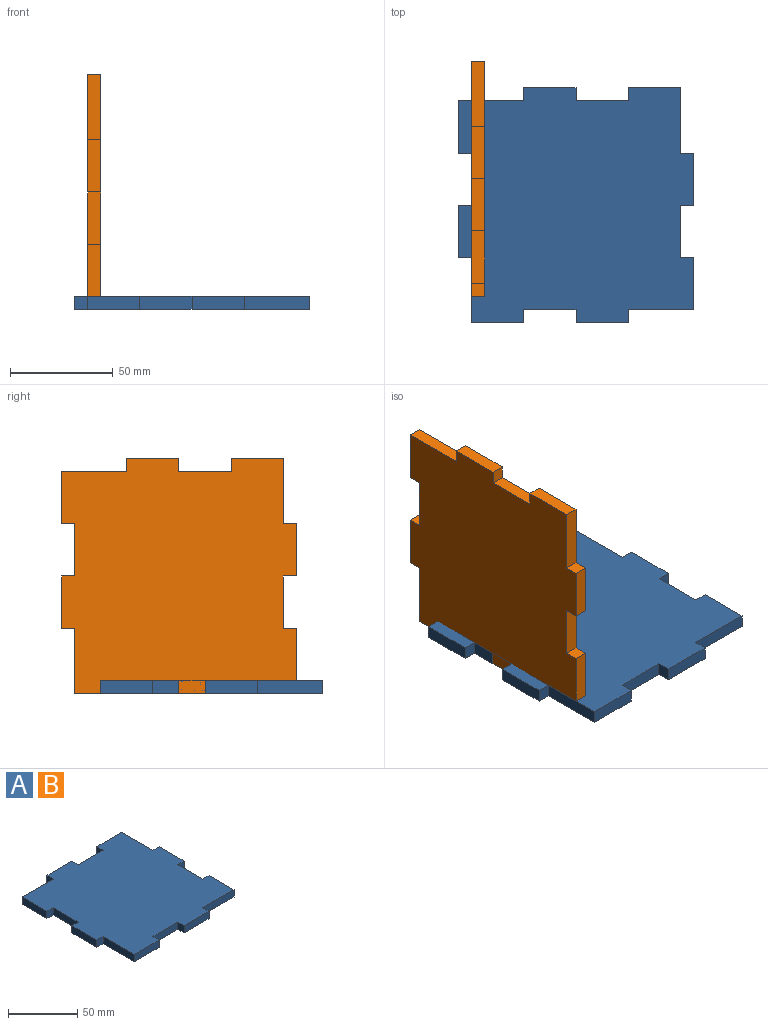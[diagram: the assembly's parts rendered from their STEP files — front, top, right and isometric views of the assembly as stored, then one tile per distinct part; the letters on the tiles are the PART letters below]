
ASSEMBLY  parts=2 mates=2
PART A: 30 faces, bbox 114.3x114.3x6.4 mm
  f0: plane 31.75x6.35mm, normal (-1,0,0), area 201.6mm2, adj f1,f27,f28,f29
  f1: plane 25.4x6.35mm, normal (0,-1,0), area 161.3mm2, adj f0,f2,f28,f29
  f2: plane 6.35x6.35mm, normal (1,0,0), area 40.3mm2, adj f1,f3,f28,f29
  f3: plane 25.4x6.35mm, normal (0,-1,0), area 161.3mm2, adj f2,f4,f28,f29
  f4: plane 6.35x6.35mm, normal (-1,0,0), area 40.3mm2, adj f3,f5,f28,f29
  f5: plane 25.4x6.35mm, normal (0,-1,0), area 161.3mm2, adj f4,f6,f28,f29
  f6: plane 6.35x6.35mm, normal (1,0,0), area 40.3mm2, adj f5,f7,f28,f29
  f7: plane 31.75x6.35mm, normal (0,-1,0), area 201.6mm2, adj f6,f8,f28,f29
  f8: plane 25.4x6.35mm, normal (1,0,0), area 161.3mm2, adj f7,f9,f28,f29
  f9: plane 6.35x6.35mm, normal (0,1,0), area 40.3mm2, adj f8,f10,f28,f29
  f10: plane 25.4x6.35mm, normal (1,0,0), area 161.3mm2, adj f9,f11,f28,f29
  f11: plane 6.35x6.35mm, normal (0,-1,0), area 40.3mm2, adj f10,f12,f28,f29
  f12: plane 25.4x6.35mm, normal (1,0,0), area 161.3mm2, adj f11,f13,f28,f29
  f13: plane 6.35x6.35mm, normal (0,1,0), area 40.3mm2, adj f12,f14,f28,f29
  f14: plane 31.75x6.35mm, normal (1,0,0), area 201.6mm2, adj f13,f15,f28,f29
  f15: plane 25.4x6.35mm, normal (0,1,0), area 161.3mm2, adj f14,f16,f28,f29
  f16: plane 6.35x6.35mm, normal (-1,0,0), area 40.3mm2, adj f15,f17,f28,f29
  f17: plane 25.4x6.35mm, normal (0,1,0), area 161.3mm2, adj f16,f18,f28,f29
  f18: plane 6.35x6.35mm, normal (1,0,0), area 40.3mm2, adj f17,f19,f28,f29
  f19: plane 25.4x6.35mm, normal (0,1,0), area 161.3mm2, adj f18,f20,f28,f29
  f20: plane 6.35x6.35mm, normal (-1,0,0), area 40.3mm2, adj f19,f21,f28,f29
  f21: plane 31.75x6.35mm, normal (0,1,0), area 201.6mm2, adj f20,f22,f28,f29
  f22: plane 25.4x6.35mm, normal (-1,0,0), area 161.3mm2, adj f21,f23,f28,f29
  f23: plane 6.35x6.35mm, normal (0,-1,0), area 40.3mm2, adj f22,f24,f28,f29
  f24: plane 25.4x6.35mm, normal (-1,0,0), area 161.3mm2, adj f23,f25,f28,f29
  f25: plane 6.35x6.35mm, normal (0,1,0), area 40.3mm2, adj f24,f26,f28,f29
  f26: plane 25.4x6.35mm, normal (-1,0,0), area 161.3mm2, adj f25,f27,f28,f29
  f27: plane 6.35x6.35mm, normal (0,-1,0), area 40.3mm2, adj f0,f26,f28,f29
  f28: plane 114.3x114.3mm, normal (0,0,1), area 11612.9mm2, adj f0,f1,f2,f3,f4,f5,f6,f7
  f29: plane 114.3x114.3mm, normal (0,0,-1), area 11612.9mm2, adj f0,f1,f2,f3,f4,f5,f6,f7
PART B: same geometry as A
PLACE A t=(7.85,63.74,-70.28)mm
PLACE B rot(axis=(0,-1,0),90deg) t=(-36.6,76.44,-13.13)mm
MATE planar B.f28 <-> A.f24  axis (-1,0,0) through (-42.95,76.44,37.67)mm
MATE planar A.f29 <-> B.f22  axis (0,0,-1) through (7.85,63.74,-70.28)mm
